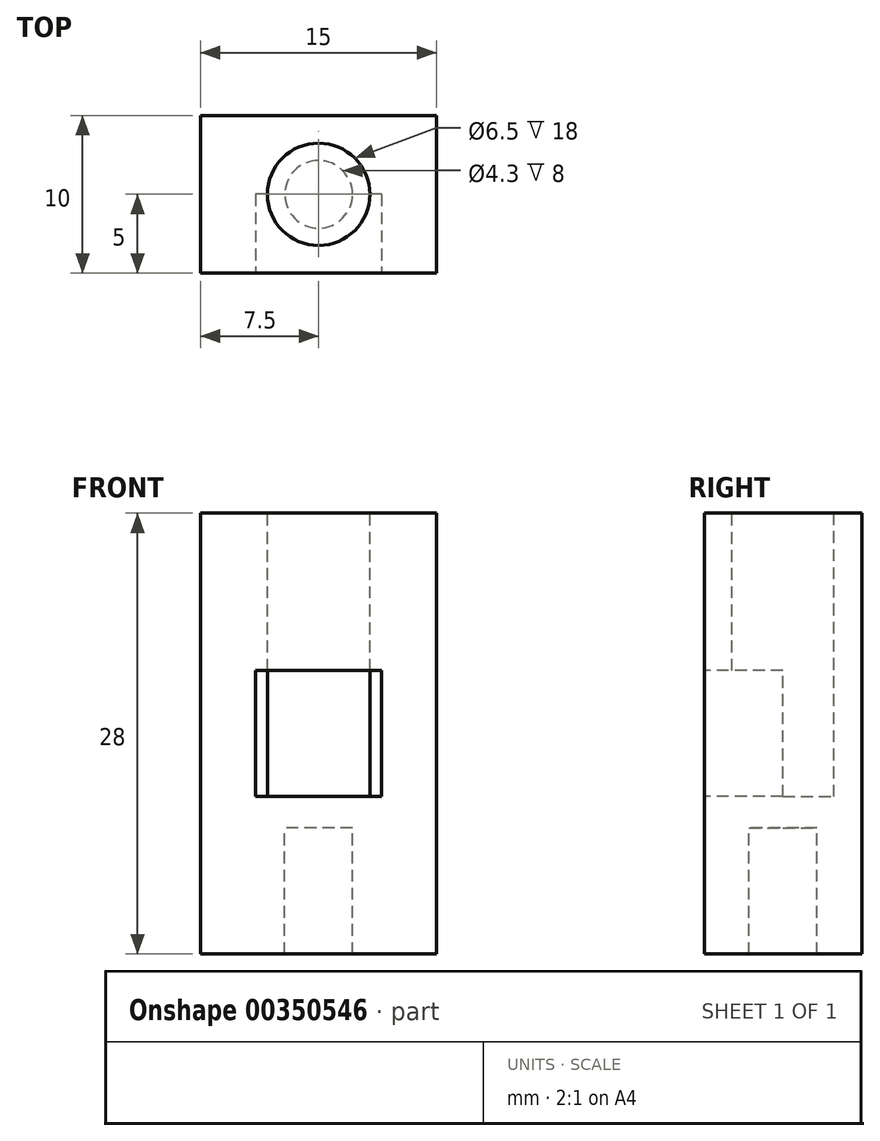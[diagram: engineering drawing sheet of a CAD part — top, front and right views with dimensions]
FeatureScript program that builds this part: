
annotation { "Feature Type Name" : "Feature", "Feature Type Description" : "" }
export const myFeature = defineFeature(function(context is Context, id is Id, definition is map)
    precondition{}
    {
        {
            var Q0;
            Q0=qCreatedBy(makeId("Top.planeOp"),FACE);
            var sketch = newSketch(context, id + "F0", { "sketchPlane" : qUnion([Q0])});
            skCircle(sketch, "E0", {"center": v(0, 0) * mm, "radius": 3 * mm});
            skCircle(sketch, "E1", {"center": v(0, 0) * mm, "radius": 2.15 * mm});
            skSolve(sketch);
        }
        {
            var Q0;
            Q0 = qSketchRegion(id + "F0", true);
            extrude(context, id + "F1", {"entities" : qUnion([Q0]), "oppositeDirection" : true, "depth" : 8 * mm});
        }
        {
            var Q0;
            Q0=makeQuery(id+"F1.opExtrude","CAP_FACE",FACE,{"disambiguationData":[OSD([sQuery(id+"F0.wireOp",EDGE,"E0"),sQuery(id+"F0.wireOp",EDGE,"E1")])],"isStart":true});
            var sketch = newSketch(context, id + "F2", { "sketchPlane" : qUnion([Q0])});
            skLineSegment(sketch, "E2.bottom", {"start": v(7.5, 5) * mm, "end": v(-7.5, 5) * mm});
            skLineSegment(sketch, "E2.top", {"start": v(7.5, -5) * mm, "end": v(-7.5, -5) * mm});
            skLineSegment(sketch, "E2.left", {"start": v(7.5, 5) * mm, "end": v(7.5, -5) * mm});
            skLineSegment(sketch, "E2.right", {"start": v(-7.5, 5) * mm, "end": v(-7.5, -5) * mm});
            skPoint(sketch, "E2.middle", {"position": v(0, 0) * mm});
            skSolve(sketch);
        }
        {
            var Q0;
            Q0 = qSketchRegion(id + "F2", true);
            extrude(context, id + "F3", {"entities" : qUnion([Q0]), "operationType" : NewBodyOperationType.ADD, "depth" : 20 * mm});
        }
        {
            var Q0;
            Q0=makeQuery(id+"F3.opExtrude","CAP_FACE",FACE,{"disambiguationData":[OSD([sQuery(id+"F2.wireOp",EDGE,"E2.bottom"),sQuery(id+"F2.wireOp",EDGE,"E2.top"),sQuery(id+"F2.wireOp",EDGE,"E2.left"),sQuery(id+"F2.wireOp",EDGE,"E2.right")])],"isStart":false});
            var sketch = newSketch(context, id + "F4", { "sketchPlane" : qUnion([Q0])});
            skCircle(sketch, "E3", {"center": v(0, 0) * mm, "radius": 3.25 * mm});
            skSolve(sketch);
        }
        {
            var Q0;
            Q0=makeQuery(id+"F3.opExtrude","SWEPT_FACE",FACE,{"disambiguationData":[OSD([sQuery(id+"F2.wireOp",EDGE,"E2.top")])]});
            var sketch = newSketch(context, id + "F5", { "sketchPlane" : qUnion([Q0])});
            skLineSegment(sketch, "E4", {"start": v(0, 0) * mm, "end": v(0, 2) * mm});
            skPoint(sketch, "E4.endSnap0", {"position": v(0, 0) * mm});
            skLineSegment(sketch, "E5", {"start": v(0, 2) * mm, "end": v(4, 2) * mm});
            skLineSegment(sketch, "E6", {"start": v(4, 2) * mm, "end": v(4, 10) * mm});
            skLineSegment(sketch, "E7", {"start": v(4, 10) * mm, "end": v(0, 10) * mm});
            skLineSegment(sketch, "E8.MirrorCS", {"start": v(-4, 10) * mm, "end": v(0, 10) * mm});
            skLineSegment(sketch, "E9.MirrorCS", {"start": v(0, 2) * mm, "end": v(-4, 2) * mm});
            skLineSegment(sketch, "E10.MirrorCS", {"start": v(-4, 2) * mm, "end": v(-4, 10) * mm});
            skSolve(sketch);
        }
        {
            var Q0;
            Q0=makeQuery(id+"F4.imprint","IMPRINT",FACE,{"disambiguationData":[TD([[makeQuery(id+"F4.imprint","IMPRINT",EDGE,{"derivedFrom":sQuery(id+"F4.wireOp",EDGE,"E3")}),1.0]])]});
            extrude(context, id + "F6", {"entities" : qUnion([Q0]), "operationType" : NewBodyOperationType.REMOVE, "oppositeDirection" : true, "depth" : 18 * mm});
        }
        {
            var Q0;
            Q0=makeQuery(id+"F5.imprint","IMPRINT",FACE,{"disambiguationData":[TD([[makeQuery(id+"F5.imprint","IMPRINT",EDGE,{"derivedFrom":sQuery(id+"F5.wireOp",EDGE,"E5")}),1.0]])]});
            extrude(context, id + "F7", {"entities" : qUnion([Q0]), "operationType" : NewBodyOperationType.REMOVE, "oppositeDirection" : true, "depth" : 5 * mm});
        }
        {
            var Q0;
            {var subQ0=sQuery(id+"F2.wireOp",EDGE,"E2.left");var subQ1=sQuery(id+"F2.wireOp",EDGE,"E2.top");var subQ2=sQuery(id+"F2.wireOp",EDGE,"E2.bottom");var subQ3=sQuery(id+"F2.wireOp",EDGE,"E2.right");Q0=makeQuery(id+"F3.boolean.opBoolean","SPLIT",FACE,{"disambiguationData":[TD([makeQuery(id+"F1.opExtrude","SWEPT_FACE",FACE,{"disambiguationData":[OSD([sQuery(id+"F0.wireOp",EDGE,"E0")])]})])],"derivedFrom":makeQuery(id+"F3.opExtrude","CAP_FACE",FACE,{"disambiguationData":[OSD([subQ2,subQ1,subQ0,subQ3])],"isStart":true})});}
            extrude(context, id + "F8", {"entities" : qUnion([Q0]), "operationType" : NewBodyOperationType.ADD, "depth" : 8 * mm});
        }
    });
